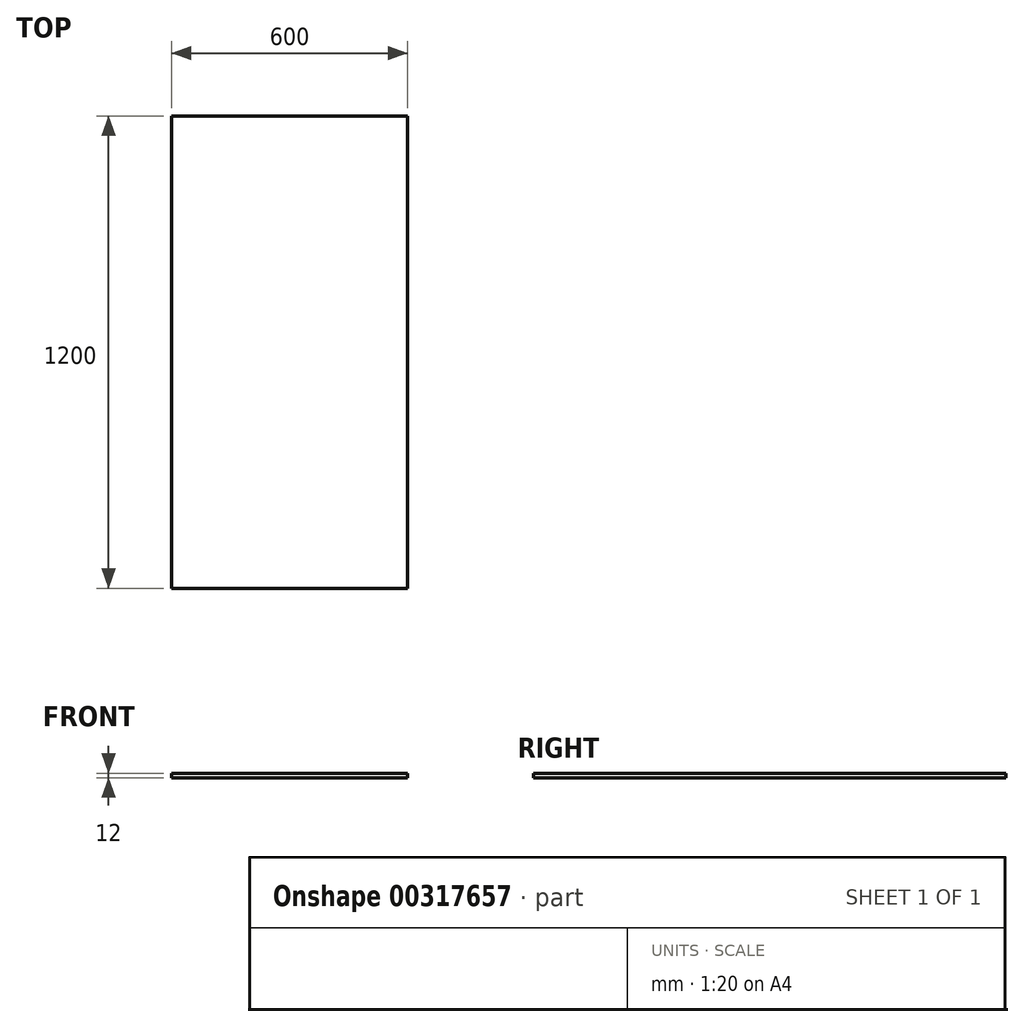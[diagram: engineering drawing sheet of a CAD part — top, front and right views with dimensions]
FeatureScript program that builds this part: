
annotation { "Feature Type Name" : "Feature", "Feature Type Description" : "" }
export const myFeature = defineFeature(function(context is Context, id is Id, definition is map)
    precondition{}
    {
        {
            var Q0;
            Q0=qCreatedBy(makeId("Front.planeOp"),FACE);
            var sketch = newSketch(context, id + "F0", { "sketchPlane" : qUnion([Q0])});
            skLineSegment(sketch, "E0.bottom", {"start": v(-33.6, 29.8) * mm, "end": v(966.4, 29.8) * mm});
            skLineSegment(sketch, "E0.top", {"start": v(-33.6, 9.8) * mm, "end": v(966.4, 9.8) * mm});
            skLineSegment(sketch, "E0.left", {"start": v(-33.6, 29.8) * mm, "end": v(-33.6, 9.8) * mm});
            skLineSegment(sketch, "E0.right", {"start": v(966.4, 29.8) * mm, "end": v(966.4, 9.8) * mm});
            skSolve(sketch);
        }
        {
            var Q0;
            Q0=qSketchRegion(id+"F0",true);
            extrude(context, id + "F1", {"entities" : qUnion([Q0]), "depth" : 2000 * mm});
        }
        {
            var Q0;
            Q0=makeQuery(id+"F1.opExtrude","SWEPT_BODY",BODY,{"disambiguationData":[OSD([sQuery(id+"F0.wireOp",EDGE,"E0.bottom"),sQuery(id+"F0.wireOp",EDGE,"E0.top"),sQuery(id+"F0.wireOp",EDGE,"E0.left"),sQuery(id+"F0.wireOp",EDGE,"E0.right")])]});
            var Q1;
            Q1=qCreatedBy(makeId("Origin.pointOp"),VERTEX);
            transform(context, id + "F2", {"entities" : qUnion([Q0]), "transformType" : TransformType.SCALE_UNIFORMLY, "scale" : .6, "scalePoint" : qUnion([Q1]), "makeCopy" : false});
        }
    });
